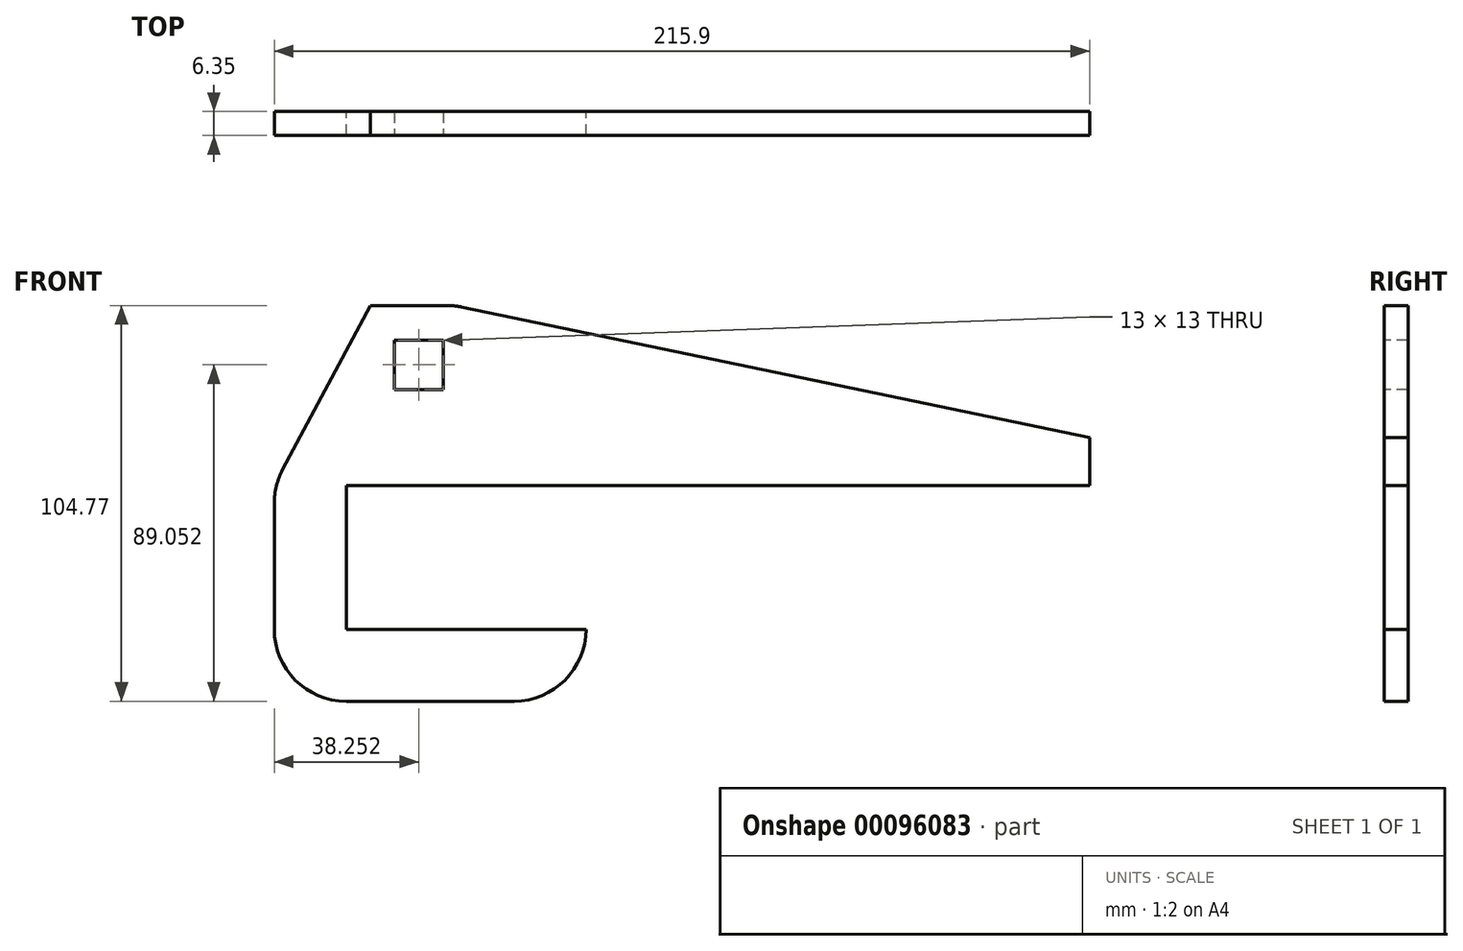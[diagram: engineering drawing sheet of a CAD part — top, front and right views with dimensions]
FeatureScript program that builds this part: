
annotation { "Feature Type Name" : "Feature", "Feature Type Description" : "" }
export const myFeature = defineFeature(function(context is Context, id is Id, definition is map)
    precondition{}
    {
        {
            var Q0;
            Q0=qCreatedBy(makeId("Front.planeOp"),FACE);
            var sketch = newSketch(context, id + "F0", { "sketchPlane" : qUnion([Q0])});
            skLineSegment(sketch, "E0", {"start": v(0, 0) * mm, "end": v(0, 57.15) * mm});
            skLineSegment(sketch, "E1", {"start": v(0, 57.15) * mm, "end": v(25.4, 104.78) * mm});
            skLineSegment(sketch, "E2", {"start": v(25.4, 104.78) * mm, "end": v(47.62, 104.78) * mm});
            skLineSegment(sketch, "E3", {"start": v(47.62, 104.78) * mm, "end": v(215.9, 69.85) * mm});
            skLineSegment(sketch, "E4", {"start": v(215.9, 69.85) * mm, "end": v(215.9, 57.15) * mm});
            skLineSegment(sketch, "E5", {"start": v(215.9, 57.15) * mm, "end": v(19.05, 57.15) * mm});
            skLineSegment(sketch, "E6", {"start": v(19.05, 57.15) * mm, "end": v(19.05, 19.05) * mm});
            skLineSegment(sketch, "E7", {"start": v(19.05, 19.05) * mm, "end": v(82.55, 19.05) * mm});
            skLineSegment(sketch, "E8", {"start": v(82.55, 19.05) * mm, "end": v(82.55, 0) * mm});
            skLineSegment(sketch, "E9", {"start": v(82.55, 0) * mm, "end": v(0, 0) * mm});
            skSolve(sketch);
        }
        {
            var Q0;
            Q0 = qSketchRegion(id + "F0", true);
            extrude(context, id + "F1", {"entities" : qUnion([Q0]), "depth" : 6.35 * mm});
        }
        {
            var Q0;
            Q0=makeQuery(id+"F1.opExtrude","CAP_FACE",FACE,{"disambiguationData":[OSD([sQuery(id+"F0.wireOp",EDGE,"E0"),sQuery(id+"F0.wireOp",EDGE,"E1"),sQuery(id+"F0.wireOp",EDGE,"E2"),sQuery(id+"F0.wireOp",EDGE,"E3"),sQuery(id+"F0.wireOp",EDGE,"E4"),sQuery(id+"F0.wireOp",EDGE,"E5"),sQuery(id+"F0.wireOp",EDGE,"E6"),sQuery(id+"F0.wireOp",EDGE,"E7"),sQuery(id+"F0.wireOp",EDGE,"E8"),sQuery(id+"F0.wireOp",EDGE,"E9")])],"isStart":false});
            var sketch = newSketch(context, id + "F2", { "sketchPlane" : qUnion([Q0])});
            skLineSegment(sketch, "E10.bottom", {"start": v(31.75, 95.55) * mm, "end": v(44.75, 95.55) * mm});
            skLineSegment(sketch, "E10.top", {"start": v(31.75, 82.55) * mm, "end": v(44.75, 82.55) * mm});
            skLineSegment(sketch, "E10.left", {"start": v(31.75, 95.55) * mm, "end": v(31.75, 82.55) * mm});
            skLineSegment(sketch, "E10.right", {"start": v(44.75, 95.55) * mm, "end": v(44.75, 82.55) * mm});
            skSolve(sketch);
        }
        {
            var Q0;
            Q0 = qSketchRegion(id + "F2", true);
            extrude(context, id + "F3", {"entities" : qUnion([Q0]), "operationType" : NewBodyOperationType.REMOVE, "endBound" : BoundingType.THROUGH_ALL, "oppositeDirection" : true, "depth" : 25.4 * mm});
        }
        {
            var Q0;
            Q0=makeQuery(id+"F1.opExtrude","SWEPT_EDGE",EDGE,{"disambiguationData":[OSD([sQuery(id+"F0.wireOp",EDGE,"E0"),sQuery(id+"F0.wireOp",EDGE,"E9")])]});
            var Q1;
            Q1=makeQuery(id+"F1.opExtrude","SWEPT_EDGE",EDGE,{"disambiguationData":[OSD([sQuery(id+"F0.wireOp",EDGE,"E8"),sQuery(id+"F0.wireOp",EDGE,"E9")])]});
            var Q2;
            Q2=makeQuery(id+"F1.opExtrude","SWEPT_EDGE",EDGE,{"disambiguationData":[OSD([sQuery(id+"F0.wireOp",EDGE,"E0"),sQuery(id+"F0.wireOp",EDGE,"E1")])]});
            var Q3;
            Q3=makeQuery(id+"F1.opExtrude","SWEPT_EDGE",EDGE,{"disambiguationData":[OSD([sQuery(id+"F0.wireOp",EDGE,"E2"),sQuery(id+"F0.wireOp",EDGE,"E3")])]});
            fillet(context, id + "F4", {"entities" : qUnion([Q0, Q1, Q2, Q3]), "radius" : 19.05 * mm, "tangentPropagation" : true, "allowEdgeOverflow" : false});
        }
    });
